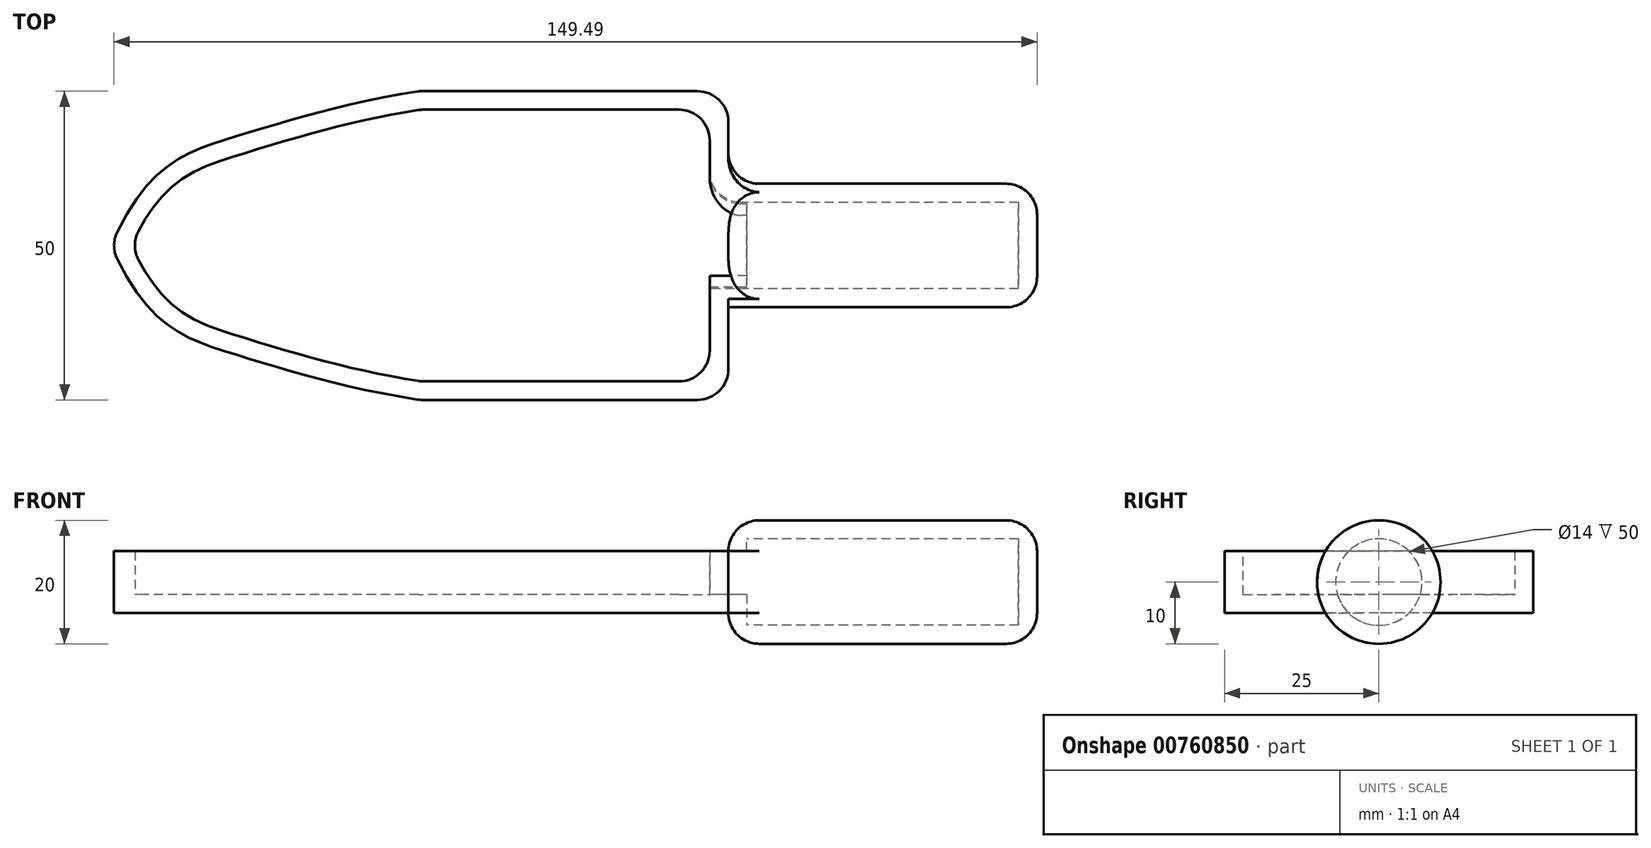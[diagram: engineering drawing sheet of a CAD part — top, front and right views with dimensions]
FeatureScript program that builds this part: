
annotation { "Feature Type Name" : "Feature", "Feature Type Description" : "" }
export const myFeature = defineFeature(function(context is Context, id is Id, definition is map)
    precondition{}
    {
        {
            var Q0;
            Q0=qCreatedBy(makeId("Top.planeOp"),FACE);
            var sketch = newSketch(context, id + "F0", { "sketchPlane" : qUnion([Q0])});
            skLineSegment(sketch, "E0.bottom", {"start": v(50, 25) * mm, "end": v(-50, 25) * mm});
            skLineSegment(sketch, "E0.top", {"start": v(50, -25) * mm, "end": v(-50, -25) * mm});
            skLineSegment(sketch, "E0.left", {"start": v(50, 25) * mm, "end": v(50, -25) * mm});
            skLineSegment(sketch, "E0.right", {"start": v(-50, 25) * mm, "end": v(-50, -25) * mm});
            skPoint(sketch, "E0.middle", {"position": v(0, 0) * mm});
            skFitSpline(sketch, "E1", {"points": [v(0, 25) * mm, v(-30.19, 17.53) * mm, v(-50, 0) * mm], "startDerivative": vector(-67.62, -10.3) * mm, "endDerivative": vector(-36.32, -82.53) * mm});
            skLineSegment(sketch, "E2", {"start": v(-50, 0) * mm, "end": v(50, 0) * mm});
            skFitSpline(sketch, "E3.MirrorCS", {"points": [v(0, -25) * mm, v(-30.19, -17.53) * mm, v(-50, 0) * mm], "startDerivative": vector(-67.62, 10.3) * mm, "endDerivative": vector(-36.32, 82.53) * mm});
            skSolve(sketch);
        }
        {
            var Q0;
            {var subQ4=sQuery(id+"F0.wireOp",EDGE,"E2");Q0=makeQuery(id+"F0.imprint","IMPRINT",FACE,{"disambiguationData":[TD([[makeQuery(id+"F0.imprint","IMPRINT",EDGE,{"derivedFrom":subQ4}),-1.0]])]});}
            var Q1;
            {var subQ3=sQuery(id+"F0.wireOp",EDGE,"E1");Q1=makeQuery(id+"F0.imprint","IMPRINT",FACE,{"disambiguationData":[TD([[makeQuery(id+"F0.imprint","IMPRINT",EDGE,{"derivedFrom":subQ3}),1.0]])]});}
            extrude(context, id + "F1", {"entities" : qUnion([Q0, Q1]), "endBound" : BoundingType.SYMMETRIC, "depth" : 10 * mm, "offsetDistance" : 25 * mm});
        }
        {
            var Q0;
            Q0=makeQuery(id+"F1.opExtrude","SWEPT_FACE",FACE,{"disambiguationData":[OSD([sQuery(id+"F0.wireOp",EDGE,"E0.left")])]});
            var sketch = newSketch(context, id + "F2", { "sketchPlane" : qUnion([Q0])});
            skCircle(sketch, "E4", {"center": v(0, 0) * mm, "radius": 10 * mm});
            skSolve(sketch);
        }
        {
            var Q0;
            Q0 = qSketchRegion(id + "F2", true);
            extrude(context, id + "F3", {"entities" : qUnion([Q0]), "operationType" : NewBodyOperationType.ADD, "depth" : 50 * mm, "offsetDistance" : 25 * mm});
        }
        {
            var Q0;
            Q0=makeQuery(id+"F1.opExtrude","CAP_FACE",FACE,{"disambiguationData":[OSD([sQuery(id+"F0.wireOp",EDGE,"E0.bottom"),sQuery(id+"F0.wireOp",EDGE,"E0.top"),sQuery(id+"F0.wireOp",EDGE,"E0.left"),sQuery(id+"F0.wireOp",EDGE,"E1"),sQuery(id+"F0.wireOp",EDGE,"E3.MirrorCS")])],"isStart":false});
            shell(context, id + "F4", {"entities" : qUnion([Q0]), "thickness" : 3 * mm});
        }
        {
            var Q0;
            Q0=makeQuery(id+"F1.opExtrude","SWEPT_EDGE",EDGE,{"disambiguationData":[OSD([sQuery(id+"F0.wireOp",EDGE,"E0.top"),sQuery(id+"F0.wireOp",EDGE,"E3.MirrorCS")])]});
            var Q1;
            Q1=makeQuery(id+"F1.opExtrude","SWEPT_EDGE",EDGE,{"disambiguationData":[OSD([sQuery(id+"F0.wireOp",EDGE,"E0.top"),sQuery(id+"F0.wireOp",EDGE,"E0.left")])]});
            var Q2;
            Q2=makeQuery(id+"F1.opExtrude","SWEPT_EDGE",EDGE,{"disambiguationData":[OSD([sQuery(id+"F0.wireOp",EDGE,"E0.bottom"),sQuery(id+"F0.wireOp",EDGE,"E0.left")])]});
            var Q3;
            Q3=makeQuery(id+"F1.opExtrude","SWEPT_EDGE",EDGE,{"disambiguationData":[OSD([sQuery(id+"F0.wireOp",EDGE,"E0.bottom"),sQuery(id+"F0.wireOp",EDGE,"E1")])]});
            var Q4;
            Q4=makeQuery(id+"F1.opExtrude","SWEPT_EDGE",EDGE,{"disambiguationData":[OSD([sQuery(id+"F0.wireOp",EDGE,"E0.right"),sQuery(id+"F0.wireOp",EDGE,"E1"),sQuery(id+"F0.wireOp",EDGE,"E2"),sQuery(id+"F0.wireOp",EDGE,"E3.MirrorCS")])]});
            fillet(context, id + "F5", {"entities" : qUnion([Q0, Q1, Q2, Q3, Q4]), "radius" : 5 * mm, "tangentPropagation" : true, "allowEdgeOverflow" : false});
        }
        {
            var Q0;
            Q0=makeQuery(id+"F4.opShell","OFFSET_EDGE",EDGE,{"disambiguationData":[OSD([sQuery(id+"F0.wireOp",EDGE,"E0.bottom"),sQuery(id+"F0.wireOp",EDGE,"E1")])]});
            var Q1;
            Q1=makeQuery(id+"F4.opShell","OFFSET_EDGE",EDGE,{"disambiguationData":[OSD([sQuery(id+"F0.wireOp",EDGE,"E0.right"),sQuery(id+"F0.wireOp",EDGE,"E1"),sQuery(id+"F0.wireOp",EDGE,"E2"),sQuery(id+"F0.wireOp",EDGE,"E3.MirrorCS")])]});
            var Q2;
            Q2=makeQuery(id+"F4.opShell","OFFSET_EDGE",EDGE,{"disambiguationData":[OSD([sQuery(id+"F0.wireOp",EDGE,"E0.top"),sQuery(id+"F0.wireOp",EDGE,"E0.left")])]});
            var Q3;
            Q3=makeQuery(id+"F4.opShell","OFFSET_EDGE",EDGE,{"disambiguationData":[OSD([sQuery(id+"F0.wireOp",EDGE,"E0.bottom"),sQuery(id+"F0.wireOp",EDGE,"E0.left")])]});
            var Q4;
            Q4=makeQuery(id+"F4.opShell","OFFSET_EDGE",EDGE,{"disambiguationData":[OSD([sQuery(id+"F0.wireOp",EDGE,"E0.top"),sQuery(id+"F0.wireOp",EDGE,"E3.MirrorCS")])]});
            fillet(context, id + "F6", {"entities" : qUnion([Q0, Q1, Q2, Q3, Q4]), "radius" : 5 * mm, "tangentPropagation" : true, "allowEdgeOverflow" : false});
        }
        {
            var Q0;
            {var subQ0=sQuery(id+"F0.wireOp",EDGE,"E0.left");var subQ1=sQuery(id+"F2.wireOp",EDGE,"E4");var subQ2=makeQuery(id+"F3.opExtrude","CAP_FACE",FACE,{"disambiguationData":[OSD([subQ1])],"isStart":true});var subQ3=makeQuery(id+"F3.opExtrude","SWEPT_FACE",FACE,{"disambiguationData":[OSD([subQ1])]});Q0=makeQuery(id+"F3.boolean.opBoolean","SPLIT",EDGE,{"disambiguationData":[topologyDisambiguationEdgeConnected([subQ3,subQ2]),TD([makeQuery(id+"F1.opExtrude","CAP_FACE",FACE,{"disambiguationData":[OSD([sQuery(id+"F0.wireOp",EDGE,"E0.bottom"),sQuery(id+"F0.wireOp",EDGE,"E0.top"),subQ0,sQuery(id+"F0.wireOp",EDGE,"E1"),sQuery(id+"F0.wireOp",EDGE,"E3.MirrorCS")])],"isStart":false})])],"derivedFrom":makeQuery(id+"F3.opExtrude","CAP_EDGE",EDGE,{"disambiguationData":[OSD([subQ1])],"isStart":true})});}
            var Q1;
            {var subQ0=sQuery(id+"F0.wireOp",EDGE,"E0.left");var subQ1=sQuery(id+"F2.wireOp",EDGE,"E4");var subQ2=makeQuery(id+"F3.opExtrude","CAP_FACE",FACE,{"disambiguationData":[OSD([subQ1])],"isStart":true});var subQ3=makeQuery(id+"F3.opExtrude","SWEPT_FACE",FACE,{"disambiguationData":[OSD([subQ1])]});Q1=makeQuery(id+"F3.boolean.opBoolean","SPLIT",EDGE,{"disambiguationData":[topologyDisambiguationEdgeConnected([subQ3,subQ2]),TD([makeQuery(id+"F1.opExtrude","CAP_FACE",FACE,{"disambiguationData":[OSD([sQuery(id+"F0.wireOp",EDGE,"E0.bottom"),sQuery(id+"F0.wireOp",EDGE,"E0.top"),subQ0,sQuery(id+"F0.wireOp",EDGE,"E1"),sQuery(id+"F0.wireOp",EDGE,"E3.MirrorCS")])],"isStart":true})])],"derivedFrom":makeQuery(id+"F3.opExtrude","CAP_EDGE",EDGE,{"disambiguationData":[OSD([subQ1])],"isStart":true})});}
            var Q2;
            Q2=makeQuery(id+"F3.opExtrude","CAP_EDGE",EDGE,{"disambiguationData":[OSD([sQuery(id+"F2.wireOp",EDGE,"E4")])],"isStart":false});
            fillet(context, id + "F7", {"entities" : qUnion([Q0, Q1, Q2]), "radius" : 5 * mm, "tangentPropagation" : true, "allowEdgeOverflow" : false});
        }
        {
            var Q0;
            {var subQ0=sQuery(id+"F2.wireOp",EDGE,"E4");Q0=makeQuery(id+"F3.boolean.opBoolean","SPLIT",EDGE,{"disambiguationData":[topologyDisambiguationEdgeConnected([makeQuery(id+"F1.opExtrude","SWEPT_FACE",FACE,{"disambiguationData":[OSD([sQuery(id+"F0.wireOp",EDGE,"E0.left")])]}),makeQuery(id+"F3.opExtrude","SWEPT_FACE",FACE,{"disambiguationData":[OSD([subQ0])]})]),OD(1.0)],"derivedFrom":makeQuery(id+"F3.opExtrude","CAP_EDGE",EDGE,{"disambiguationData":[OSD([subQ0])],"isStart":true})});}
            var Q1;
            {var subQ0=sQuery(id+"F2.wireOp",EDGE,"E4");Q1=makeQuery(id+"F3.boolean.opBoolean","SPLIT",EDGE,{"disambiguationData":[topologyDisambiguationEdgeConnected([makeQuery(id+"F1.opExtrude","SWEPT_FACE",FACE,{"disambiguationData":[OSD([sQuery(id+"F0.wireOp",EDGE,"E0.left")])]}),makeQuery(id+"F3.opExtrude","SWEPT_FACE",FACE,{"disambiguationData":[OSD([subQ0])]})]),OD(0.0)],"derivedFrom":makeQuery(id+"F3.opExtrude","CAP_EDGE",EDGE,{"disambiguationData":[OSD([subQ0])],"isStart":true})});}
            var Q2;
            {var subQ0=sQuery(id+"F2.wireOp",EDGE,"E4");Q2=makeQuery(id+"F4.opShell","OFFSET_EDGE",EDGE,{"disambiguationData":[OSD([subQ0]),TDD([makeQuery(id+"F3.boolean.opBoolean","SPLIT",EDGE,{"disambiguationData":[topologyDisambiguationEdgeConnected([makeQuery(id+"F1.opExtrude","SWEPT_FACE",FACE,{"disambiguationData":[OSD([sQuery(id+"F0.wireOp",EDGE,"E0.left")])]}),makeQuery(id+"F3.opExtrude","SWEPT_FACE",FACE,{"disambiguationData":[OSD([subQ0])]})]),OD(0.0)],"derivedFrom":makeQuery(id+"F3.opExtrude","CAP_EDGE",EDGE,{"disambiguationData":[OSD([subQ0])],"isStart":true})})])]});}
            var Q3;
            {var subQ0=sQuery(id+"F2.wireOp",EDGE,"E4");Q3=makeQuery(id+"F4.opShell","OFFSET_EDGE",EDGE,{"disambiguationData":[OSD([subQ0]),TDD([makeQuery(id+"F3.boolean.opBoolean","SPLIT",EDGE,{"disambiguationData":[topologyDisambiguationEdgeConnected([makeQuery(id+"F1.opExtrude","SWEPT_FACE",FACE,{"disambiguationData":[OSD([sQuery(id+"F0.wireOp",EDGE,"E0.left")])]}),makeQuery(id+"F3.opExtrude","SWEPT_FACE",FACE,{"disambiguationData":[OSD([subQ0])]})]),OD(1.0)],"derivedFrom":makeQuery(id+"F3.opExtrude","CAP_EDGE",EDGE,{"disambiguationData":[OSD([subQ0])],"isStart":true})})])]});}
            fillet(context, id + "F8", {"entities" : qUnion([Q0, Q1, Q2, Q3]), "radius" : 5 * mm, "tangentPropagation" : true, "allowEdgeOverflow" : false});
        }
    });
